# Revit family: M_Kombinowana zaokrąglona góra z przycięciem
name_source: partatom
category: Windows
revit_build: Autodesk Revit 2014 (Build: 20130126_1515(x64)
units: mm (PartAtom-declared; Revit-internal decimal feet)

## types (4) — shared parameters
Analytic Construction = Duże pojedynczo szklone okna
Construction Type Id = SGL
Heat Transfer Coefficient (U) = 5.5617 W/(m²·K)
Materiał szyby = Szkło
Przycięcie materiału - wewnętrzne = Przycięcie
Przycięcie materiału - zewnętrzne = Przycięcie
Rama okienna = Rama okienna
Rzut przycięcia - wewnętrzny = 19 mm  [stored 0.062336 ft]
Rzut przycięcia - zewnętrzny = 13 mm  [stored 0.0426509 ft]
Solar Heat Gain Coefficient = 0.86
Szerokość przycięcia - wewnętrzna = 89 mm  [stored 0.291995 ft]
Szerokość przycięcia - zewnętrzna = 89 mm  [stored 0.291995 ft]
Visual Light Transmittance = 0.9
Wall Closure = By host
Wstawka okna = 19 mm  [stored 0.062336 ft]

## per-type parameters (varying)
| type | Domyślna wysokość parapetu | Height | Width |
| 0915 x 1830 mm | 305 mm  [stored 1.00066 ft] | 1830 mm  [stored 6.00394 ft] | 915 mm  [stored 3.00197 ft] |
| 0915 x 1220 mm | 915 mm  [stored 3.00197 ft] | 1220 mm | 915 mm  [stored 3.00197 ft] |
| 1220 x 1220 mm | 915 mm  [stored 3.00197 ft] | 1220 mm | 1220 mm |
| 1220 x 1830 mm | 305 mm  [stored 1.00066 ft] | 1830 mm  [stored 6.00394 ft] | 1220 mm |

note: [stored X ft] marks values corroborated as IEEE doubles in the binary element streams (Revit-internal decimal feet)
